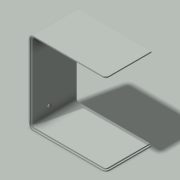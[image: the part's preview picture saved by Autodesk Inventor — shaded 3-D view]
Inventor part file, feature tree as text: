
AUTODESK INVENTOR PART (.ipt)
format: ipt  version: 2015 (Build 190159000, 159)  size: 157,184 bytes
history: native  units: in
note: dims shown in document units (in); Inventor stores cm internally (conversion verified against a paired STEP export)
features: other x3, reference x3, extrude x2, fillet x2, sketch x2, plane x1, chamfer x1
ambient origin geometry x8: Origin, YZ Plane, XZ Plane, XY Plane, X Axis, Y Axis, Z Axis, Center Point
bodies: Solid1 (feature_tree)
feature tree (14):
  plane  "Work Plane1"
  extrude  "Extrusion1"  Depth=0.0787in
  other  "Lip1"
  other  "Lip4"
  other  "Lip5"
  fillet  "Fillet1"  Radius=1.4567in
  fillet  "Fillet4"  Radius=0.0787in
  extrude  "Extrusion2"  Depth=0.1181in
  chamfer  "Chamfer1"  Distance=0.3937in
  sketch  "Sketch1"  dims[d0=0.0787in d1=0.1575in d2=1.4567in d3=0.0in]
  reference  "Reference1"
  sketch  "Sketch2"  dims[d4=0.0394in d5=0.0394in d6=0.0in d7=0.0in d8=0.0in d9=0.0in d22=0.0787in d25=0.1181in d26=0.0394in d27=0.0394in d28=0.0in d29=0.0in d30=0.0in d31=0.0in d32=0.0394in d33=0.0394in d34=0.0in d35=0.0in d36=0.0in d37=0.0in d38=0.3937in d39=0.0in d40=0.0394in d41=0.0787in d42=45.0deg]
  reference  "Reference2"
  reference  "Reference3"
